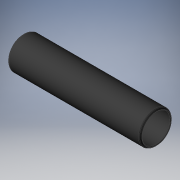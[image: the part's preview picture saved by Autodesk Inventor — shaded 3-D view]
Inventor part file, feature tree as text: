
AUTODESK INVENTOR PART (.ipt)
format: ipt  version: 2019 (Build 230136000, 136)  size: 163,840 bytes
history: native  units: in
note: dims shown in document units (in); Inventor stores cm internally (conversion verified against a paired STEP export)
features: other x42, revolve x1, sketch x1
ambient origin geometry x8: Origin, YZ Plane, XZ Plane, XY Plane, X Axis, Y Axis, Z Axis, Center Point
bodies: Solid1 (feature_tree)
feature tree (44):
  revolve  "Revolution1"  [1 undecoded]
  other  "cp1_XY"
  other  "cp1_YZ"
  other  "cp1_ZX"
  other  "cp1_X"
  other  "cp1_Y"
  other  "cp1_Z"
  other  "cp1_Center"
  other  "cp2_XY"
  other  "cp2_YZ"
  other  "cp2_ZX"
  other  "cp2_X"
  other  "cp2_Y"
  other  "cp2_Z"
  other  "cp2_Center"
  other  "cp3_XY"
  other  "cp3_YZ"
  other  "cp3_ZX"
  other  "cp3_X"
  other  "cp3_Y"
  other  "cp3_Z"
  other  "cp3_Center"
  other  "cp4_XY"
  other  "cp4_YZ"
  other  "cp4_ZX"
  other  "cp4_X"
  other  "cp4_Y"
  other  "cp4_Z"
  other  "cp4_Center"
  other  "tube_front_XY"
  other  "tube_front_YZ"
  other  "tube_front_ZX"
  other  "tube_front_X"
  other  "tube_front_Y"
  other  "tube_front_Z"
  other  "tube_front_Center"
  other  "tube_rear_XY"
  other  "tube_rear_YZ"
  other  "tube_rear_ZX"
  other  "tube_rear_X"
  other  "tube_rear_Y"
  other  "tube_rear_Z"
  other  "tube_rear_Center"
  sketch  "Sketch_1"  dims[d0=360.0deg]
note: 1 required parameter value undecoded (feature->parameter linkage not recoverable at this tier; creation-order binding heuristic only, values carry confidence <= 0.55)
